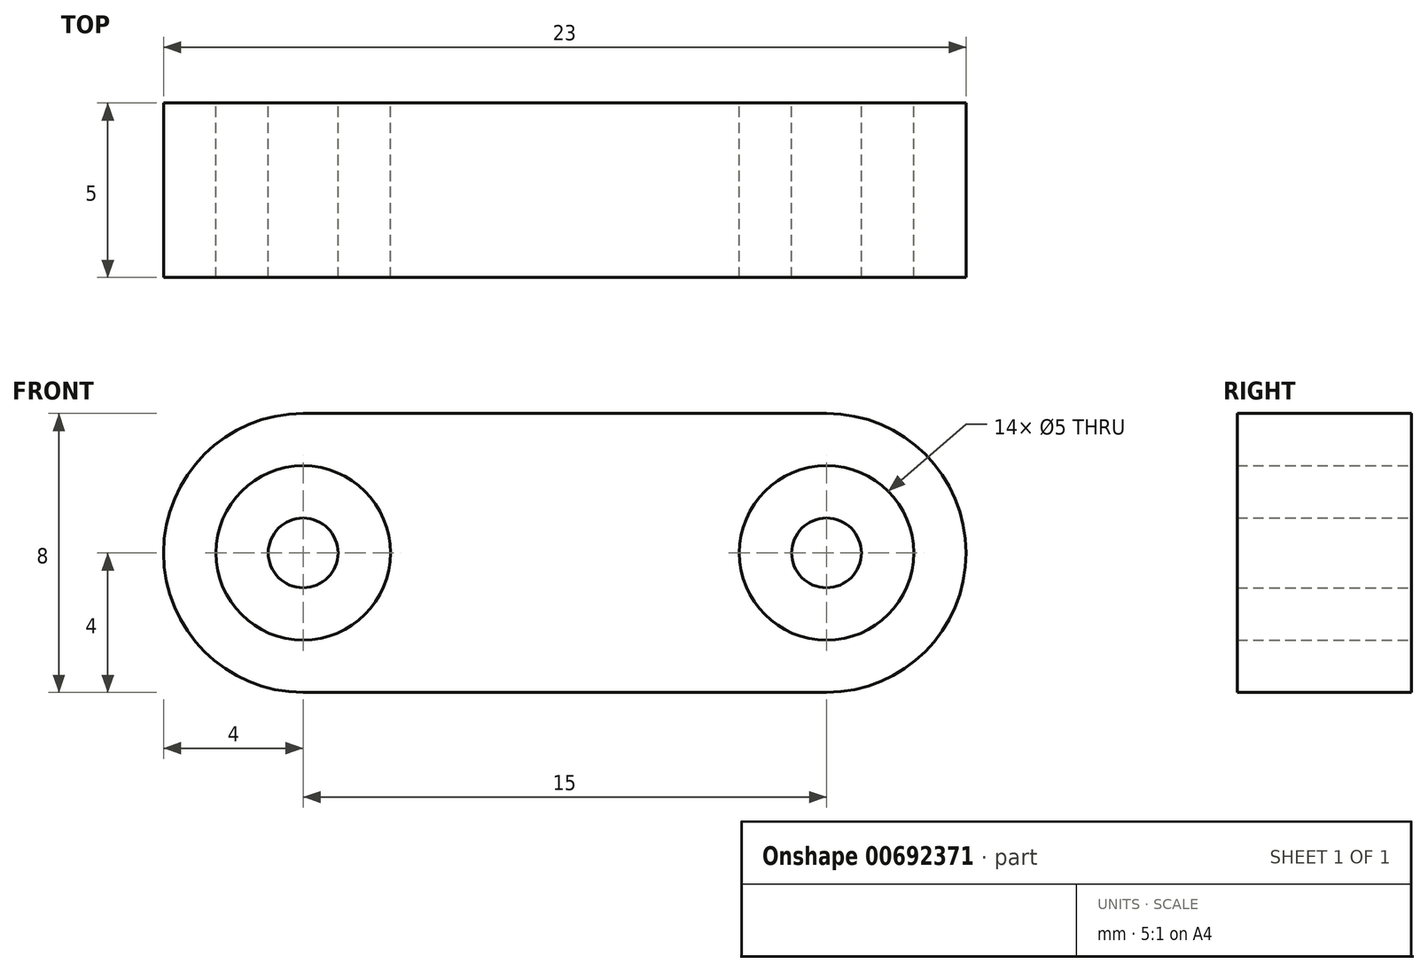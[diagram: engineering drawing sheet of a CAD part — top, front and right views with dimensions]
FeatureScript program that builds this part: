
annotation { "Feature Type Name" : "Feature", "Feature Type Description" : "" }
export const myFeature = defineFeature(function(context is Context, id is Id, definition is map)
    precondition{}
    {
        {
            var Q0;
            Q0=qCreatedBy(makeId("Front.planeOp"),FACE);
            var sketch = newSketch(context, id + "F0", { "sketchPlane" : qUnion([Q0])});
            skArc(sketch, "E0", {"start": v(-15, 4) * mm, "mid": v(-19, 0) * mm, "end": v(-15, -4) * mm});
            skArc(sketch, "E1", {"start": v(0, -4) * mm, "mid": v(4, 0) * mm, "end": v(0, 4) * mm});
            skLineSegment(sketch, "E2", {"start": v(-15, 4) * mm, "end": v(0, 4) * mm});
            skLineSegment(sketch, "E3", {"start": v(-15, -4) * mm, "end": v(0, -4) * mm});
            skCircle(sketch, "E4", {"center": v(-15, 0) * mm, "radius": 2.5 * mm});
            skCircle(sketch, "E5", {"center": v(0, 0) * mm, "radius": 2.5 * mm});
            skCircle(sketch, "E6", {"center": v(-15, 0) * mm, "radius": 1 * mm});
            skCircle(sketch, "E7", {"center": v(0, 0) * mm, "radius": 1 * mm});
            skSolve(sketch);
        }
        {
            var Q0;
            Q0 = qSketchRegion(id + "F0", true);
            var Q1;
            Q1=makeQuery(id+"F0.imprint","IMPRINT",FACE,{"disambiguationData":[TD([[makeQuery(id+"F0.imprint","IMPRINT",EDGE,{"derivedFrom":sQuery(id+"F0.wireOp",EDGE,"E6")}),1.0]])]});
            var Q2;
            Q2=makeQuery(id+"F0.imprint","IMPRINT",FACE,{"disambiguationData":[TD([[makeQuery(id+"F0.imprint","IMPRINT",EDGE,{"derivedFrom":sQuery(id+"F0.wireOp",EDGE,"E7")}),1.0]])]});
            extrude(context, id + "F1", {"entities" : qUnion([Q0, Q1, Q2]), "depth" : 5 * mm, "offsetDistance" : 25 * mm});
        }
    });
